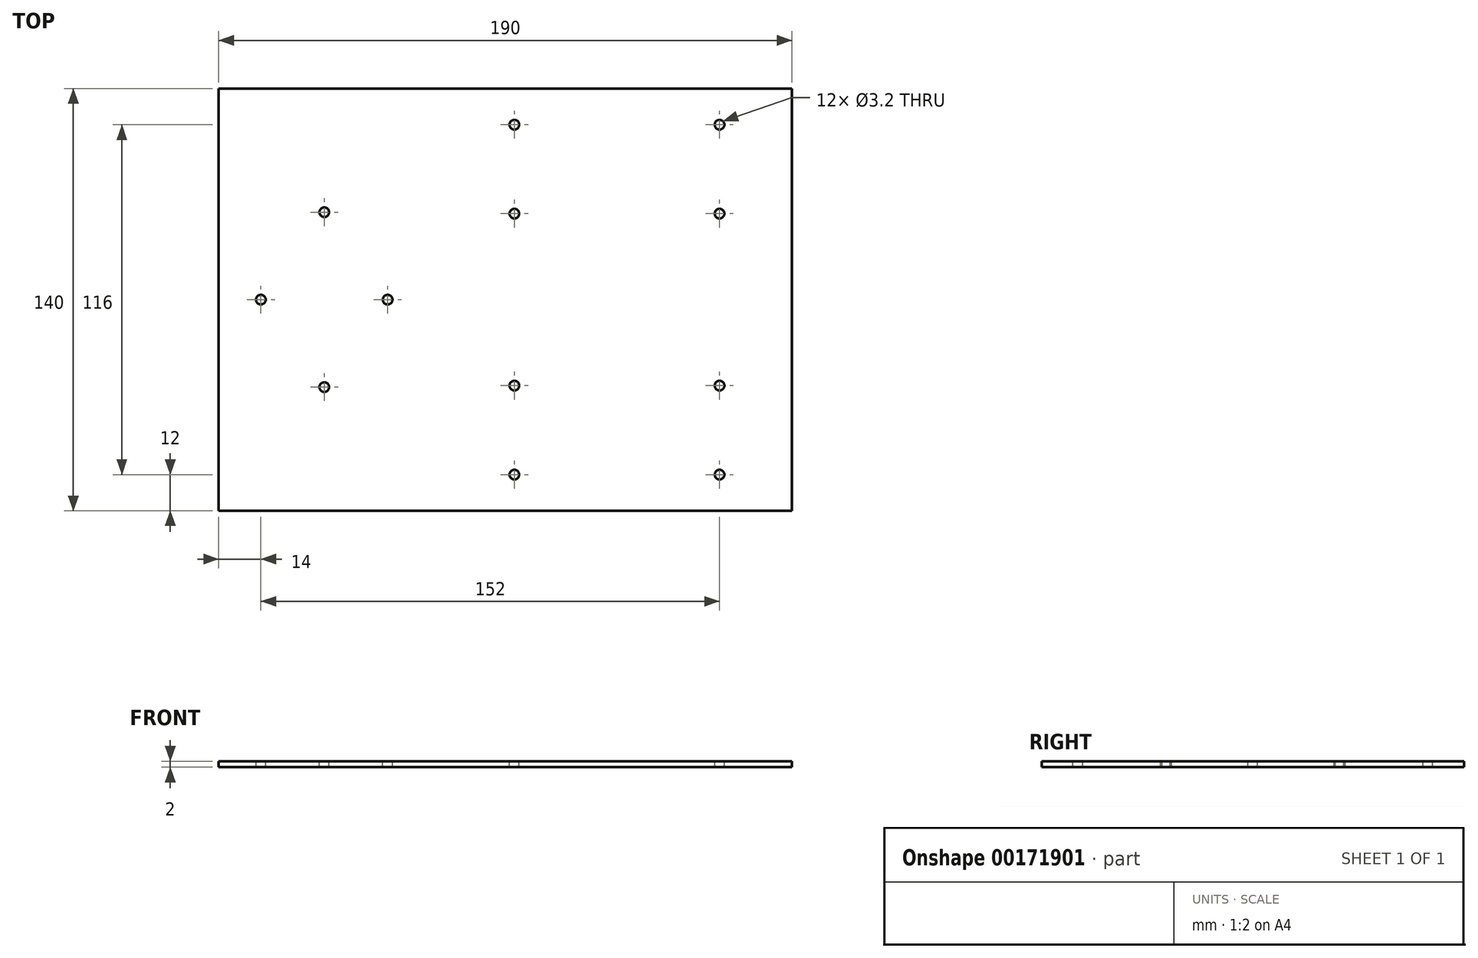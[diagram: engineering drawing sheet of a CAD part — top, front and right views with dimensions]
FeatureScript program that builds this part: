
annotation { "Feature Type Name" : "Feature", "Feature Type Description" : "" }
export const myFeature = defineFeature(function(context is Context, id is Id, definition is map)
    precondition{}
    {
        {
            var Q0;
            Q0=qCreatedBy(makeId("Top.planeOp"),FACE);
            var sketch = newSketch(context, id + "F0", { "sketchPlane" : qUnion([Q0])});
            skLineSegment(sketch, "E0.bottom", {"start": v(-95, 70) * mm, "end": v(95, 70) * mm});
            skLineSegment(sketch, "E0.top", {"start": v(-95, -70) * mm, "end": v(95, -70) * mm});
            skLineSegment(sketch, "E0.left", {"start": v(-95, 70) * mm, "end": v(-95, -70) * mm});
            skLineSegment(sketch, "E0.right", {"start": v(95, 70) * mm, "end": v(95, -70) * mm});
            skPoint(sketch, "E0.middle", {"position": v(0, 0) * mm});
            skSolve(sketch);
        }
        {
            var Q0;
            Q0 = qSketchRegion(id + "F0", true);
            extrude(context, id + "F1", {"entities" : qUnion([Q0]), "depth" : 2 * mm});
        }
        {
            var Q0;
            Q0=makeQuery(id+"F1.opExtrude","CAP_FACE",FACE,{"disambiguationData":[OSD([sQuery(id+"F0.wireOp",EDGE,"E0.bottom"),sQuery(id+"F0.wireOp",EDGE,"E0.top"),sQuery(id+"F0.wireOp",EDGE,"E0.left"),sQuery(id+"F0.wireOp",EDGE,"E0.right")])],"isStart":false});
            var sketch = newSketch(context, id + "F2", { "sketchPlane" : qUnion([Q0])});
            skCircle(sketch, "E1", {"center": v(71, 58) * mm, "radius": 1.6 * mm});
            skCircle(sketch, "E2", {"center": v(71, 28.5) * mm, "radius": 1.6 * mm});
            skCircle(sketch, "E3", {"center": v(3, 58) * mm, "radius": 1.6 * mm});
            skCircle(sketch, "E4", {"center": v(3, 28.5) * mm, "radius": 1.6 * mm});
            skCircle(sketch, "E5.MirrorC", {"center": v(71, -28.5) * mm, "radius": 1.6 * mm});
            skCircle(sketch, "E6.MirrorC", {"center": v(3, -28.5) * mm, "radius": 1.6 * mm});
            skCircle(sketch, "E7.MirrorC", {"center": v(3, -58) * mm, "radius": 1.6 * mm});
            skCircle(sketch, "E8.MirrorC", {"center": v(71, -58) * mm, "radius": 1.6 * mm});
            skCircle(sketch, "E9", {"center": v(-81, 0) * mm, "radius": 1.6 * mm});
            skCircle(sketch, "E10", {"center": v(-39, 0) * mm, "radius": 1.6 * mm});
            skLineSegment(sketch, "E11", {"start": v(-81, 0) * mm, "end": v(-60, 0) * mm});
            skCircle(sketch, "E12", {"center": v(-60, 29) * mm, "radius": 1.6 * mm});
            skCircle(sketch, "E13.MirrorC", {"center": v(-60, -29) * mm, "radius": 1.6 * mm});
            skSolve(sketch);
        }
        {
            var Q0;
            Q0 = qSketchRegion(id + "F2", true);
            extrude(context, id + "F3", {"entities" : qUnion([Q0]), "operationType" : NewBodyOperationType.REMOVE, "oppositeDirection" : true, "depth" : 25 * mm});
        }
    });
